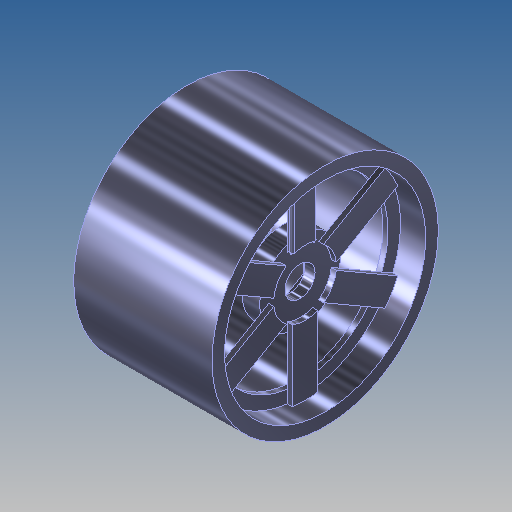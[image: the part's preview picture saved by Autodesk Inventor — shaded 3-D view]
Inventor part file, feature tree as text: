
AUTODESK INVENTOR PART (.ipt)
format: ipt  version: 2020 (Build 240168000, 168)  size: 306,688 bytes
history: native  units: mm
features: extrude x5, sketch x5, other x2, fillet x1, pattern_circular x1
ambient origin geometry x8: Origin, YZ Plane, XZ Plane, XY Plane, X Axis, Y Axis, Z Axis, Center Point
bodies: Body1 (feature_tree)
feature tree (14):
  other  "Твердое тело1"
  extrude  "Выдавливание1"  Depth=90.0mm
  other  "РабПлоскость1"
  extrude  "Выдавливание2"  Depth=5.0mm
  extrude  "Выдавливание3"  Depth=55.0mm TaperAngle=0.0deg
  extrude  "Выдавливание4"  [1 undecoded]
  fillet  "Сопряжение1"  Radius=5.0mm
  pattern_circular  "Круговой массив1"  [2 undecoded]
  extrude  "Выдавливание5"  Depth=12.0mm
  sketch  "Эскиз1"
  sketch  "Эскиз2"
  sketch  "Эскиз3"
  sketch  "Эскиз4"
  sketch  "Эскиз5"
note: 3 required parameter values undecoded (feature->parameter linkage not recoverable at this tier; creation-order binding heuristic only, values carry confidence <= 0.55)
